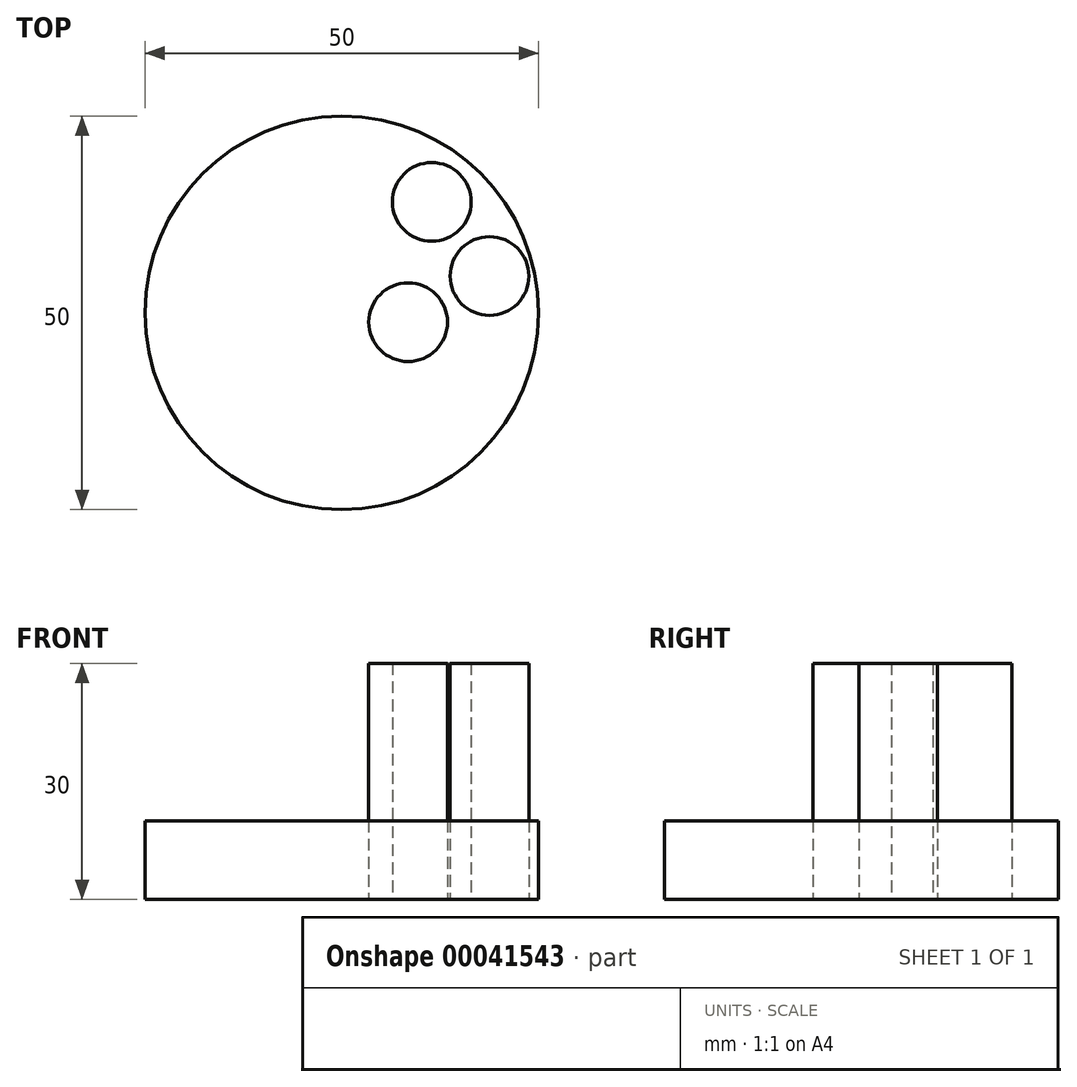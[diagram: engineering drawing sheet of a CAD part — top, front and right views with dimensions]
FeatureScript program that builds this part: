
annotation { "Feature Type Name" : "Feature", "Feature Type Description" : "" }
export const myFeature = defineFeature(function(context is Context, id is Id, definition is map)
    precondition{}
    {
        {
            var Q0;
            Q0=qCreatedBy(makeId("Top.planeOp"),FACE);
            var sketch = newSketch(context, id + "F0", { "sketchPlane" : qUnion([Q0])});
            skCircle(sketch, "E0", {"center": v(0, 0) * mm, "radius": 25 * mm});
            skCircle(sketch, "E1", {"center": v(-41.24, -27.3) * mm, "radius": 10 * mm});
            skCircle(sketch, "E2", {"center": v(53.15, -5.78) * mm, "radius": 10 * mm});
            skCircle(sketch, "E3", {"center": v(27.73, 38.74) * mm, "radius": 5 * mm});
            skCircle(sketch, "E4", {"center": v(35.51, -28.24) * mm, "radius": 7.5 * mm});
            skCircle(sketch, "E5", {"center": v(-20.1, 25.92) * mm, "radius": 5 * mm});
            skCircle(sketch, "E6", {"center": v(48.67, 28.4) * mm, "radius": 5 * mm});
            skSolve(sketch);
        }
        {
            var Q0;
            Q0=makeQuery(id+"F0.imprint","IMPRINT",FACE,{"disambiguationData":[TD([[makeQuery(id+"F0.imprint","IMPRINT",EDGE,{"derivedFrom":sQuery(id+"F0.wireOp",EDGE,"E0")}),1.0]])]});
            extrude(context, id + "F1", {"entities" : qUnion([Q0]), "depth" : 10 * mm});
        }
        {
            var Q0;
            Q0=qCreatedBy(makeId("Top.planeOp"),FACE);
            var sketch = newSketch(context, id + "F2", { "sketchPlane" : qUnion([Q0])});
            skCircle(sketch, "E7", {"center": v(11.43, 14.1) * mm, "radius": 5 * mm});
            skCircle(sketch, "E8", {"center": v(18.77, 4.69) * mm, "radius": 5 * mm});
            skCircle(sketch, "E9", {"center": v(8.43, -1.17) * mm, "radius": 5 * mm});
            skSolve(sketch);
        }
        {
            var Q0;
            Q0=makeQuery(id+"F2.imprint","IMPRINT",FACE,{"disambiguationData":[TD([[makeQuery(id+"F2.imprint","IMPRINT",EDGE,{"derivedFrom":sQuery(id+"F2.wireOp",EDGE,"E8")}),1.0]])]});
            var Q1;
            Q1=makeQuery(id+"F2.imprint","IMPRINT",FACE,{"disambiguationData":[TD([[makeQuery(id+"F2.imprint","IMPRINT",EDGE,{"derivedFrom":sQuery(id+"F2.wireOp",EDGE,"E7")}),1.0]])]});
            var Q2;
            Q2=makeQuery(id+"F2.imprint","IMPRINT",FACE,{"disambiguationData":[TD([[makeQuery(id+"F2.imprint","IMPRINT",EDGE,{"derivedFrom":sQuery(id+"F2.wireOp",EDGE,"E9")}),1.0]])]});
            extrude(context, id + "F3", {"entities" : qUnion([Q0, Q1, Q2]), "depth" : 30 * mm});
        }
    });
